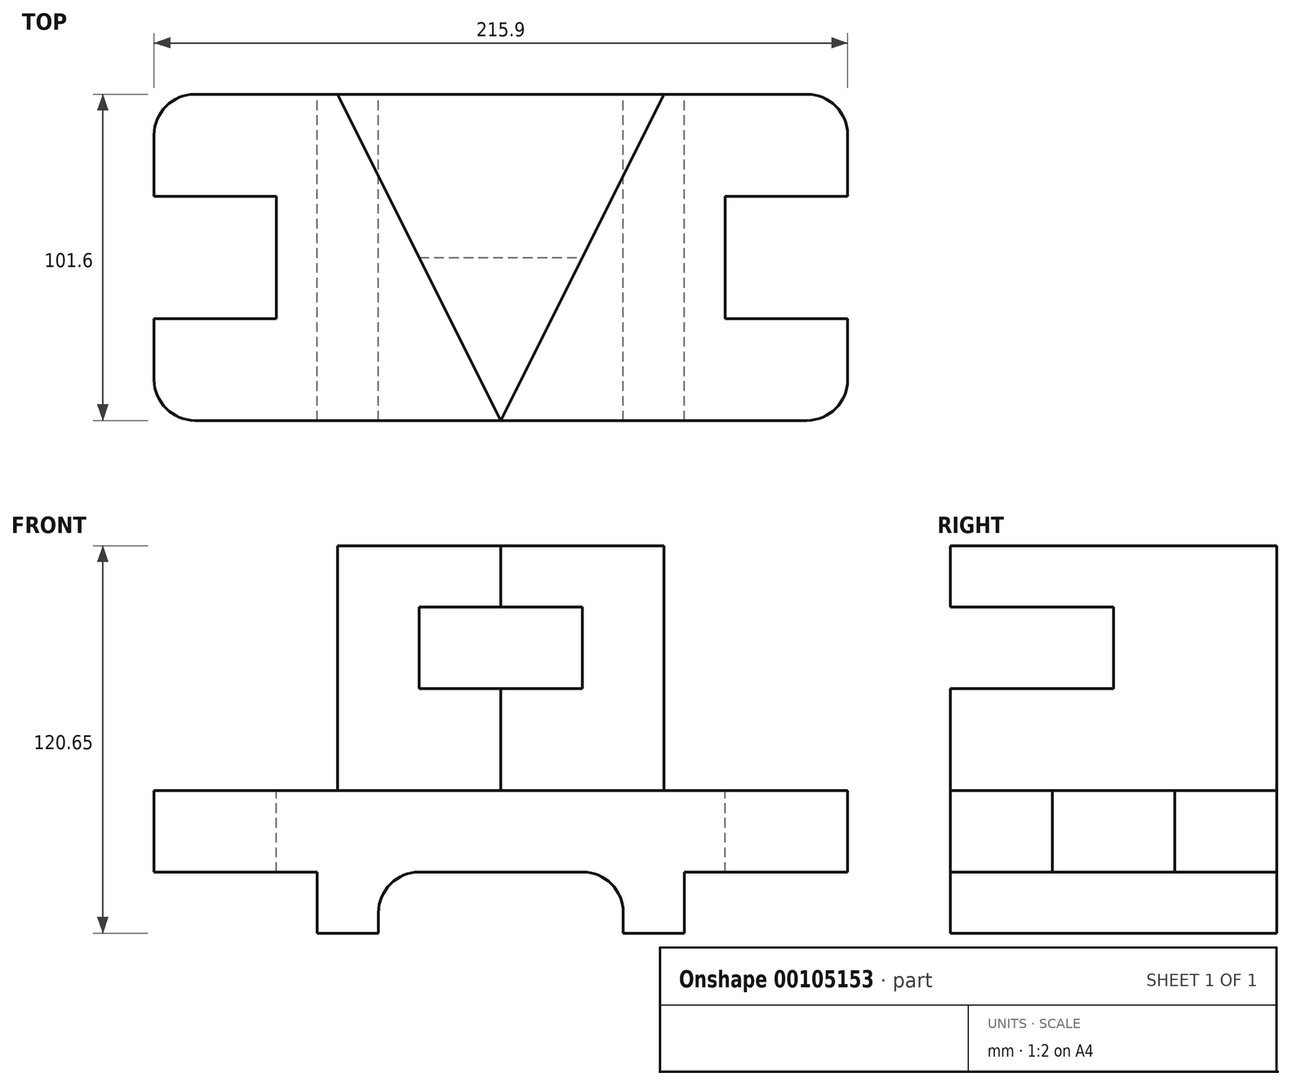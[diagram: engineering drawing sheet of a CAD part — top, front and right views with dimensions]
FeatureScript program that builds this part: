
annotation { "Feature Type Name" : "Feature", "Feature Type Description" : "" }
export const myFeature = defineFeature(function(context is Context, id is Id, definition is map)
    precondition{}
    {
        {
            var Q0;
            Q0=qCreatedBy(makeId("Front.planeOp"),FACE);
            var sketch = newSketch(context, id + "F0", { "sketchPlane" : qUnion([Q0])});
            skLineSegment(sketch, "E0.bottom", {"start": v(-107.95, 0) * mm, "end": v(107.95, 0) * mm});
            skLineSegment(sketch, "E0.top", {"start": v(-107.95, -25.4) * mm, "end": v(-57.15, -25.4) * mm});
            skLineSegment(sketch, "E0.left", {"start": v(-107.95, 0) * mm, "end": v(-107.95, -25.4) * mm});
            skLineSegment(sketch, "E0.right", {"start": v(107.95, 0) * mm, "end": v(107.95, -25.4) * mm});
            skLineSegment(sketch, "E1", {"start": v(-57.15, -25.4) * mm, "end": v(-57.15, -44.45) * mm});
            skLineSegment(sketch, "E2", {"start": v(-57.15, -44.45) * mm, "end": v(-38.1, -44.45) * mm});
            skLineSegment(sketch, "E3", {"start": v(-38.1, -44.45) * mm, "end": v(-38.1, -38.1) * mm});
            skArc(sketch, "E4", {"start": v(-25.4, -25.4) * mm, "mid": v(-34.38, -29.12) * mm, "end": v(-38.1, -38.1) * mm});
            skLineSegment(sketch, "E5", {"start": v(57.15, -25.4) * mm, "end": v(57.15, -44.45) * mm});
            skLineSegment(sketch, "E6", {"start": v(57.15, -44.45) * mm, "end": v(38.1, -44.45) * mm});
            skLineSegment(sketch, "E7", {"start": v(38.1, -44.45) * mm, "end": v(38.1, -38.1) * mm});
            skArc(sketch, "E8", {"start": v(38.1, -38.1) * mm, "mid": v(34.38, -29.12) * mm, "end": v(25.4, -25.4) * mm});
            skLineSegment(sketch, "E9.trimOffspring", {"start": v(-25.4, -25.4) * mm, "end": v(25.4, -25.4) * mm});
            skLineSegment(sketch, "E10.trimOffspring", {"start": v(57.15, -25.4) * mm, "end": v(107.95, -25.4) * mm});
            skSolve(sketch);
        }
        {
            var Q0;
            Q0 = qSketchRegion(id + "F0", true);
            extrude(context, id + "F1", {"entities" : qUnion([Q0]), "depth" : 101.6 * mm});
        }
        {
            var Q0;
            Q0=makeQuery(id+"F1.opExtrude","SWEPT_FACE",FACE,{"disambiguationData":[OSD([sQuery(id+"F0.wireOp",EDGE,"E0.bottom")])]});
            var sketch = newSketch(context, id + "F2", { "sketchPlane" : qUnion([Q0])});
            skLineSegment(sketch, "E11", {"start": v(-95.25, 0) * mm, "end": v(-95.25, -12.7) * mm, "construction": true});
            skLineSegment(sketch, "E12", {"start": v(95.25, 0) * mm, "end": v(95.25, -12.7) * mm, "construction": true});
            skLineSegment(sketch, "E13", {"start": v(-107.95, -12.7) * mm, "end": v(-95.25, -12.7) * mm, "construction": true});
            skLineSegment(sketch, "E14", {"start": v(-107.95, -88.9) * mm, "end": v(-95.25, -88.9) * mm, "construction": true});
            skArc(sketch, "E15", {"start": v(-95.25, 0) * mm, "mid": v(-104.23, -3.72) * mm, "end": v(-107.95, -12.7) * mm});
            skArc(sketch, "E16", {"start": v(-107.95, -88.9) * mm, "mid": v(-104.23, -97.88) * mm, "end": v(-95.25, -101.6) * mm});
            skArc(sketch, "E17", {"start": v(95.25, -101.6) * mm, "mid": v(104.23, -97.88) * mm, "end": v(107.95, -88.9) * mm});
            skArc(sketch, "E18", {"start": v(107.95, -12.7) * mm, "mid": v(104.23, -3.72) * mm, "end": v(95.25, 0) * mm});
            skLineSegment(sketch, "E19.trimOffspring", {"start": v(95.25, -12.7) * mm, "end": v(107.95, -12.7) * mm, "construction": true});
            skLineSegment(sketch, "E20.trimOffspring", {"start": v(-95.25, -88.9) * mm, "end": v(-95.25, -101.6) * mm, "construction": true});
            skLineSegment(sketch, "E21.trimOffspring", {"start": v(95.25, -88.9) * mm, "end": v(107.95, -88.9) * mm, "construction": true});
            skLineSegment(sketch, "E22.trimOffspring", {"start": v(95.25, -88.9) * mm, "end": v(95.25, -101.6) * mm, "construction": true});
            skLineSegment(sketch, "E23", {"start": v(-107.95, -12.7) * mm, "end": v(-107.95, 0) * mm});
            skLineSegment(sketch, "E24", {"start": v(-107.95, 0) * mm, "end": v(-95.25, 0) * mm});
            skLineSegment(sketch, "E25", {"start": v(-107.95, -88.9) * mm, "end": v(-107.95, -101.6) * mm});
            skLineSegment(sketch, "E26", {"start": v(-107.95, -101.6) * mm, "end": v(-95.25, -101.6) * mm});
            skLineSegment(sketch, "E27", {"start": v(95.25, -101.6) * mm, "end": v(107.95, -101.6) * mm});
            skLineSegment(sketch, "E28", {"start": v(107.95, -101.6) * mm, "end": v(107.95, -88.9) * mm});
            skLineSegment(sketch, "E29", {"start": v(107.95, -12.7) * mm, "end": v(107.95, 0) * mm});
            skLineSegment(sketch, "E30", {"start": v(107.95, 0) * mm, "end": v(95.25, 0) * mm});
            skLineSegment(sketch, "E31.bottom", {"start": v(-107.95, -31.75) * mm, "end": v(-69.85, -31.75) * mm});
            skLineSegment(sketch, "E31.top", {"start": v(-107.95, -69.85) * mm, "end": v(-69.85, -69.85) * mm});
            skLineSegment(sketch, "E31.left", {"start": v(-107.95, -31.75) * mm, "end": v(-107.95, -69.85) * mm});
            skLineSegment(sketch, "E31.right", {"start": v(-69.85, -31.75) * mm, "end": v(-69.85, -69.85) * mm});
            skLineSegment(sketch, "E32.bottom", {"start": v(107.95, -31.75) * mm, "end": v(69.85, -31.75) * mm});
            skLineSegment(sketch, "E32.top", {"start": v(107.95, -69.85) * mm, "end": v(69.85, -69.85) * mm});
            skLineSegment(sketch, "E32.left", {"start": v(107.95, -31.75) * mm, "end": v(107.95, -69.85) * mm});
            skLineSegment(sketch, "E32.right", {"start": v(69.85, -31.75) * mm, "end": v(69.85, -69.85) * mm});
            skSolve(sketch);
        }
        {
            var Q0;
            Q0 = qSketchRegion(id + "F2", true);
            extrude(context, id + "F3", {"entities" : qUnion([Q0]), "operationType" : NewBodyOperationType.REMOVE, "endBound" : BoundingType.THROUGH_ALL, "oppositeDirection" : true, "depth" : 25.4 * mm});
        }
        {
            var Q0;
            Q0=makeQuery(id+"F1.opExtrude","SWEPT_FACE",FACE,{"disambiguationData":[OSD([sQuery(id+"F0.wireOp",EDGE,"E0.bottom")])]});
            var sketch = newSketch(context, id + "F4", { "sketchPlane" : qUnion([Q0])});
            skLineSegment(sketch, "E33", {"start": v(0, -101.6) * mm, "end": v(50.8, 0) * mm});
            skLineSegment(sketch, "E34", {"start": v(50.8, 0) * mm, "end": v(-50.8, 0) * mm});
            skLineSegment(sketch, "E35", {"start": v(-50.8, 0) * mm, "end": v(0, -101.6) * mm});
            skSolve(sketch);
        }
        {
            var Q0;
            Q0 = qSketchRegion(id + "F4", true);
            extrude(context, id + "F5", {"entities" : qUnion([Q0]), "operationType" : NewBodyOperationType.ADD, "depth" : 76.2 * mm});
        }
        {
            var Q0;
            Q0=qCreatedBy(makeId("Right.planeOp"),FACE);
            var sketch = newSketch(context, id + "F6", { "sketchPlane" : qUnion([Q0])});
            skLineSegment(sketch, "E36.bottom", {"start": v(-101.6, 57.15) * mm, "end": v(-50.8, 57.15) * mm});
            skLineSegment(sketch, "E36.top", {"start": v(-101.6, 31.75) * mm, "end": v(-50.8, 31.75) * mm});
            skLineSegment(sketch, "E36.left", {"start": v(-101.6, 57.15) * mm, "end": v(-101.6, 31.75) * mm});
            skLineSegment(sketch, "E36.right", {"start": v(-50.8, 57.15) * mm, "end": v(-50.8, 31.75) * mm});
            skSolve(sketch);
        }
        {
            var Q0;
            Q0 = qSketchRegion(id + "F6", true);
            extrude(context, id + "F7", {"entities" : qUnion([Q0]), "operationType" : NewBodyOperationType.REMOVE, "endBound" : BoundingType.THROUGH_ALL, "oppositeDirection" : true, "depth" : 25.4 * mm, "hasSecondDirection" : true, "secondDirectionBound" : SecondDirectionBoundingType.THROUGH_ALL, "secondDirectionOppositeDirection" : false, "secondDirectionDepth" : 25.4 * mm});
        }
    });
